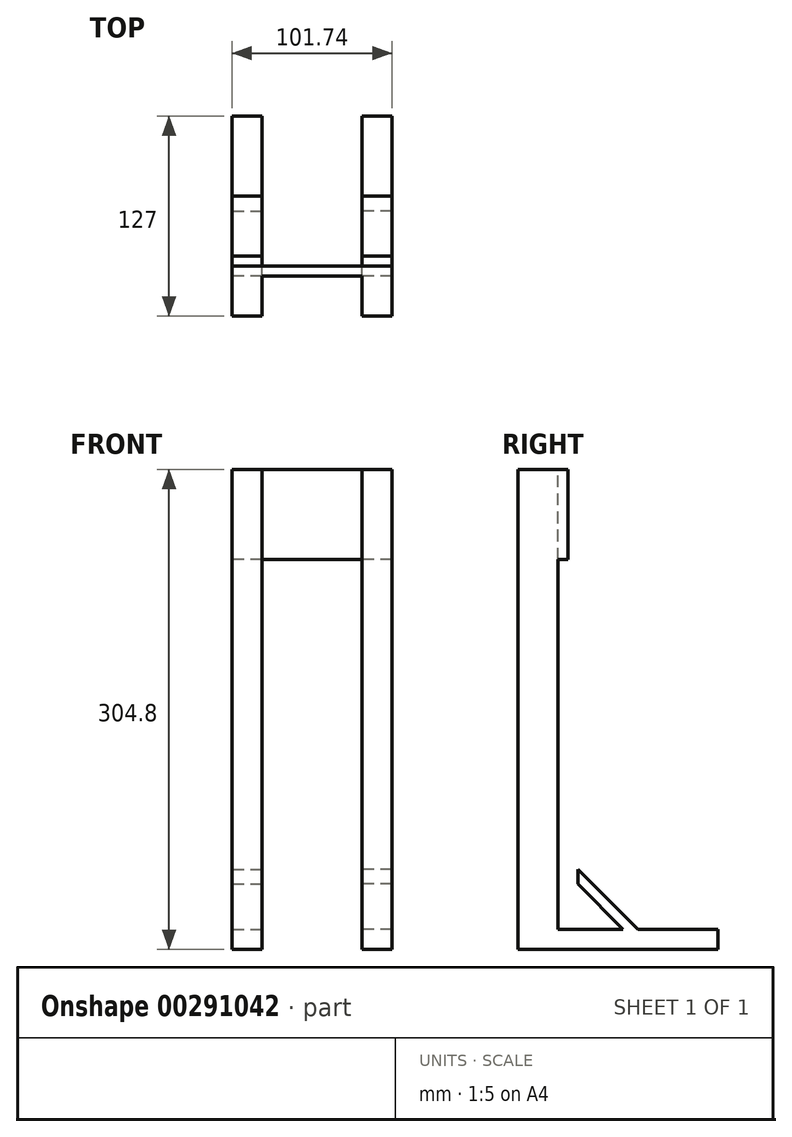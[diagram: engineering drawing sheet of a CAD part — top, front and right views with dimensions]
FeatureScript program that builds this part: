
annotation { "Feature Type Name" : "Feature", "Feature Type Description" : "" }
export const myFeature = defineFeature(function(context is Context, id is Id, definition is map)
    precondition{}
    {
        {
            var Q0;
            Q0=qCreatedBy(makeId("Right.planeOp"),FACE);
            var sketch = newSketch(context, id + "F0", { "sketchPlane" : qUnion([Q0])});
            skLineSegment(sketch, "E0.bottom", {"start": v(0, 0) * mm, "end": v(101.6, 0) * mm});
            skLineSegment(sketch, "E0.top", {"start": v(0, 12.7) * mm, "end": v(101.6, 12.7) * mm});
            skLineSegment(sketch, "E0.left", {"start": v(0, 0) * mm, "end": v(0, 12.7) * mm});
            skLineSegment(sketch, "E0.right", {"start": v(101.6, 0) * mm, "end": v(101.6, 12.7) * mm});
            skLineSegment(sketch, "E1.bottom", {"start": v(0, 0) * mm, "end": v(-25.4, 0) * mm});
            skLineSegment(sketch, "E1.top", {"start": v(0, 304.8) * mm, "end": v(-25.4, 304.8) * mm});
            skLineSegment(sketch, "E1.left", {"start": v(0, 0) * mm, "end": v(0, 304.8) * mm});
            skLineSegment(sketch, "E1.right", {"start": v(-25.4, 0) * mm, "end": v(-25.4, 304.8) * mm});
            skLineSegment(sketch, "E2.bottom", {"start": v(0, 12.7) * mm, "end": v(12.7, 12.7) * mm});
            skLineSegment(sketch, "E2.top", {"start": v(0, 88.9) * mm, "end": v(12.7, 88.9) * mm});
            skLineSegment(sketch, "E2.left", {"start": v(0, 12.7) * mm, "end": v(0, 88.9) * mm});
            skLineSegment(sketch, "E2.right", {"start": v(12.7, 12.7) * mm, "end": v(12.7, 88.9) * mm});
            skLineSegment(sketch, "E3", {"start": v(12.7, 50.8) * mm, "end": v(50.8, 12.7) * mm});
            skLineSegment(sketch, "E4.0", {"start": v(12.7, 41.77) * mm, "end": v(41.21, 12.7) * mm});
            skSolve(sketch);
        }
        {
            var Q0;
            {var subQ3=sQuery(id+"F0.wireOp",EDGE,"E1.bottom");Q0=makeQuery(id+"F0.imprint","IMPRINT",FACE,{"disambiguationData":[TD([[makeQuery(id+"F0.imprint","IMPRINT",EDGE,{"derivedFrom":subQ3}),-1.0]])]});}
            var Q1;
            {var subQ1=sQuery(id+"F0.wireOp",EDGE,"E2.bottom");Q1=makeQuery(id+"F0.imprint","IMPRINT",FACE,{"disambiguationData":[TD([[makeQuery(id+"F0.imprint","IMPRINT",EDGE,{"derivedFrom":subQ1}),1.0]])]});}
            var Q2;
            {var subQ0=sQuery(id+"F0.wireOp",EDGE,"E3");Q2=makeQuery(id+"F0.imprint","IMPRINT",FACE,{"disambiguationData":[TD([[makeQuery(id+"F0.imprint","IMPRINT",EDGE,{"derivedFrom":subQ0}),-1.0]])]});}
            var Q3;
            {var subQ5=sQuery(id+"F0.wireOp",EDGE,"E0.bottom");Q3=makeQuery(id+"F0.imprint","IMPRINT",FACE,{"disambiguationData":[TD([[makeQuery(id+"F0.imprint","IMPRINT",EDGE,{"derivedFrom":subQ5}),1.0]])]});}
            extrude(context, id + "F1", {"entities" : qUnion([Q0, Q1, Q2, Q3]), "endBound" : BoundingType.SYMMETRIC, "depth" : 19.05 * mm});
        }
        {
            var Q0;
            Q0=makeQuery(id+"F1.opExtrude","CAP_FACE",FACE,{"disambiguationData":[OSD([sQuery(id+"F0.wireOp",EDGE,"E0.bottom"),sQuery(id+"F0.wireOp",EDGE,"E0.top"),sQuery(id+"F0.wireOp",EDGE,"E0.right"),sQuery(id+"F0.wireOp",EDGE,"E1.bottom"),sQuery(id+"F0.wireOp",EDGE,"E1.top"),sQuery(id+"F0.wireOp",EDGE,"E1.left"),sQuery(id+"F0.wireOp",EDGE,"E1.right"),sQuery(id+"F0.wireOp",EDGE,"E2.top"),sQuery(id+"F0.wireOp",EDGE,"E2.right"),sQuery(id+"F0.wireOp",EDGE,"E3"),sQuery(id+"F0.wireOp",EDGE,"E4.0")])],"isStart":true});
            cPlane(context, id + "F2", {"entities" : qUnion([Q0]), "cplaneType" : CPlaneType.OFFSET, "offset" : 31.75 * mm, "width" : 152.4 * mm, "height" : 152.4 * mm});
        }
        {
            var Q0;
            Q0=makeQuery(id+"F1.opExtrude","SWEPT_BODY",BODY,{"disambiguationData":[OSD([sQuery(id+"F0.wireOp",EDGE,"E0.bottom"),sQuery(id+"F0.wireOp",EDGE,"E0.top"),sQuery(id+"F0.wireOp",EDGE,"E0.right"),sQuery(id+"F0.wireOp",EDGE,"E1.bottom"),sQuery(id+"F0.wireOp",EDGE,"E1.top"),sQuery(id+"F0.wireOp",EDGE,"E1.left"),sQuery(id+"F0.wireOp",EDGE,"E1.right"),sQuery(id+"F0.wireOp",EDGE,"E2.top"),sQuery(id+"F0.wireOp",EDGE,"E2.right"),sQuery(id+"F0.wireOp",EDGE,"E3"),sQuery(id+"F0.wireOp",EDGE,"E4.0")])]});
            var Q1;
            Q1=qCreatedBy(id+"F2.planeOp",FACE);
            mirror(context, id + "F3", {"entities" : qUnion([Q0]), "mirrorPlane" : qUnion([Q1])});
        }
        {
            var Q0;
            {var subQ0=sQuery(id+"F0.wireOp",EDGE,"E2.right");Q0=makeQuery(id+"F3.opPattern","COPY",FACE,{"derivedFrom":makeQuery(id+"F1.opExtrude","SWEPT_FACE",FACE,{"disambiguationData":[OSD([subQ0]),TDD([makeQuery(id+"F0.imprint","IMPRINT",EDGE,{"disambiguationData":[TD([[makeQuery(id+"F0.imprint","INTERSECT",VERTEX,{"derivedFrom":[sQuery(id+"F0.wireOp",EDGE,"E2.top"),subQ0]}),1.0]])],"derivedFrom":subQ0})])]}),"instanceName":"1"});}
            var sketch = newSketch(context, id + "F4", { "sketchPlane" : qUnion([Q0])});
            skCircle(sketch, "E5", {"center": v(82.11, 77.64) * mm, "radius": 2.36 * mm});
            skCircle(sketch, "E6.MirrorC", {"center": v(0.44, 77.64) * mm, "radius": 2.36 * mm});
            skSolve(sketch);
        }
        {
            var Q0;
            Q0=sQuery(id+"F4.wireOp",VERTEX,"E6.MirrorC.center");
            var Q1;
            Q1=sQuery(id+"F4.wireOp",VERTEX,"E5.center");
            var Q2;
            Q2=makeQuery(id+"F1.opExtrude","SWEPT_BODY",BODY,{"disambiguationData":[OSD([sQuery(id+"F0.wireOp",EDGE,"E0.bottom"),sQuery(id+"F0.wireOp",EDGE,"E0.top"),sQuery(id+"F0.wireOp",EDGE,"E0.right"),sQuery(id+"F0.wireOp",EDGE,"E1.bottom"),sQuery(id+"F0.wireOp",EDGE,"E1.top"),sQuery(id+"F0.wireOp",EDGE,"E1.left"),sQuery(id+"F0.wireOp",EDGE,"E1.right"),sQuery(id+"F0.wireOp",EDGE,"E2.top"),sQuery(id+"F0.wireOp",EDGE,"E2.right"),sQuery(id+"F0.wireOp",EDGE,"E3"),sQuery(id+"F0.wireOp",EDGE,"E4.0")])]});
            var Q3;
            Q3=makeQuery(id+"F3.opPattern","COPY",BODY,{"derivedFrom":makeQuery(id+"F1.opExtrude","SWEPT_BODY",BODY,{"disambiguationData":[OSD([sQuery(id+"F0.wireOp",EDGE,"E0.bottom"),sQuery(id+"F0.wireOp",EDGE,"E0.top"),sQuery(id+"F0.wireOp",EDGE,"E0.right"),sQuery(id+"F0.wireOp",EDGE,"E1.bottom"),sQuery(id+"F0.wireOp",EDGE,"E1.top"),sQuery(id+"F0.wireOp",EDGE,"E1.left"),sQuery(id+"F0.wireOp",EDGE,"E1.right"),sQuery(id+"F0.wireOp",EDGE,"E2.top"),sQuery(id+"F0.wireOp",EDGE,"E2.right"),sQuery(id+"F0.wireOp",EDGE,"E3"),sQuery(id+"F0.wireOp",EDGE,"E4.0")])]}),"instanceName":"1"});
            hole(context, id + "F5", {"style" : HoleStyle.SIMPLE, "endStyle" : HoleEndStyle.THROUGH, "holeDiameter" : 2.54 * mm, "tappedDepth" : 12.7 * mm, "tapClearance" : 3, "locations" : qUnion([Q0, Q1]), "scope" : qUnion([Q2, Q3])});
        }
        {
            var Q0;
            Q0=makeQuery(id+"F1.opExtrude","SWEPT_FACE",FACE,{"disambiguationData":[OSD([sQuery(id+"F0.wireOp",EDGE,"E1.left")])]});
            var sketch = newSketch(context, id + "F6", { "sketchPlane" : qUnion([Q0])});
            skLineSegment(sketch, "E7.bottom", {"start": v(-9.52, 304.8) * mm, "end": v(92.2, 304.8) * mm});
            skLineSegment(sketch, "E7.top", {"start": v(-9.52, 285.64) * mm, "end": v(92.2, 285.64) * mm});
            skLineSegment(sketch, "E7.left", {"start": v(-9.53, 304.8) * mm, "end": v(-9.53, 285.64) * mm});
            skLineSegment(sketch, "E7.right", {"start": v(92.2, 304.8) * mm, "end": v(92.2, 285.64) * mm});
            skLineSegment(sketch, "E8.top", {"start": v(-9.52, 267.26) * mm, "end": v(92.2, 267.26) * mm});
            skLineSegment(sketch, "E8.left", {"start": v(-9.52, 285.64) * mm, "end": v(-9.52, 267.26) * mm});
            skLineSegment(sketch, "E8.right", {"start": v(92.2, 285.64) * mm, "end": v(92.2, 267.26) * mm});
            skLineSegment(sketch, "E9.top", {"start": v(-9.52, 247.63) * mm, "end": v(92.2, 247.63) * mm});
            skLineSegment(sketch, "E9.left", {"start": v(-9.52, 267.26) * mm, "end": v(-9.52, 247.63) * mm});
            skLineSegment(sketch, "E9.right", {"start": v(92.2, 267.26) * mm, "end": v(92.2, 247.63) * mm});
            skSolve(sketch);
        }
        {
            var Q0;
            {var subQ3=sQuery(id+"F6.wireOp",EDGE,"E7.right");Q0=makeQuery(id+"F6.imprint","IMPRINT",FACE,{"disambiguationData":[TD([[makeQuery(id+"F6.imprint","IMPRINT",EDGE,{"derivedFrom":subQ3}),-1.0]])]});}
            var Q1;
            {var subQ0=sQuery(id+"F6.wireOp",EDGE,"E8.right");Q1=makeQuery(id+"F6.imprint","IMPRINT",FACE,{"disambiguationData":[TD([[makeQuery(id+"F6.imprint","IMPRINT",EDGE,{"derivedFrom":subQ0}),-1.0]])]});}
            var Q2;
            {var subQ0=sQuery(id+"F6.wireOp",EDGE,"E9.right");Q2=makeQuery(id+"F6.imprint","IMPRINT",FACE,{"disambiguationData":[TD([[makeQuery(id+"F6.imprint","IMPRINT",EDGE,{"derivedFrom":subQ0}),-1.0]])]});}
            var Q3;
            {var subQ3=sQuery(id+"F6.wireOp",EDGE,"E7.left");Q3=makeQuery(id+"F6.imprint","IMPRINT",FACE,{"disambiguationData":[TD([[makeQuery(id+"F6.imprint","IMPRINT",EDGE,{"derivedFrom":subQ3}),-1.0]])]});}
            var Q4;
            {var subQ0=sQuery(id+"F6.wireOp",EDGE,"E8.left");Q4=makeQuery(id+"F6.imprint","IMPRINT",FACE,{"disambiguationData":[TD([[makeQuery(id+"F6.imprint","IMPRINT",EDGE,{"derivedFrom":subQ0}),-1.0]])]});}
            var Q5;
            {var subQ0=sQuery(id+"F6.wireOp",EDGE,"E9.left");Q5=makeQuery(id+"F6.imprint","IMPRINT",FACE,{"disambiguationData":[TD([[makeQuery(id+"F6.imprint","IMPRINT",EDGE,{"derivedFrom":subQ0}),-1.0]])]});}
            extrude(context, id + "F7", {"entities" : qUnion([Q0, Q1, Q2, Q3, Q4, Q5]), "operationType" : NewBodyOperationType.ADD, "depth" : 6.35 * mm});
        }
    });
